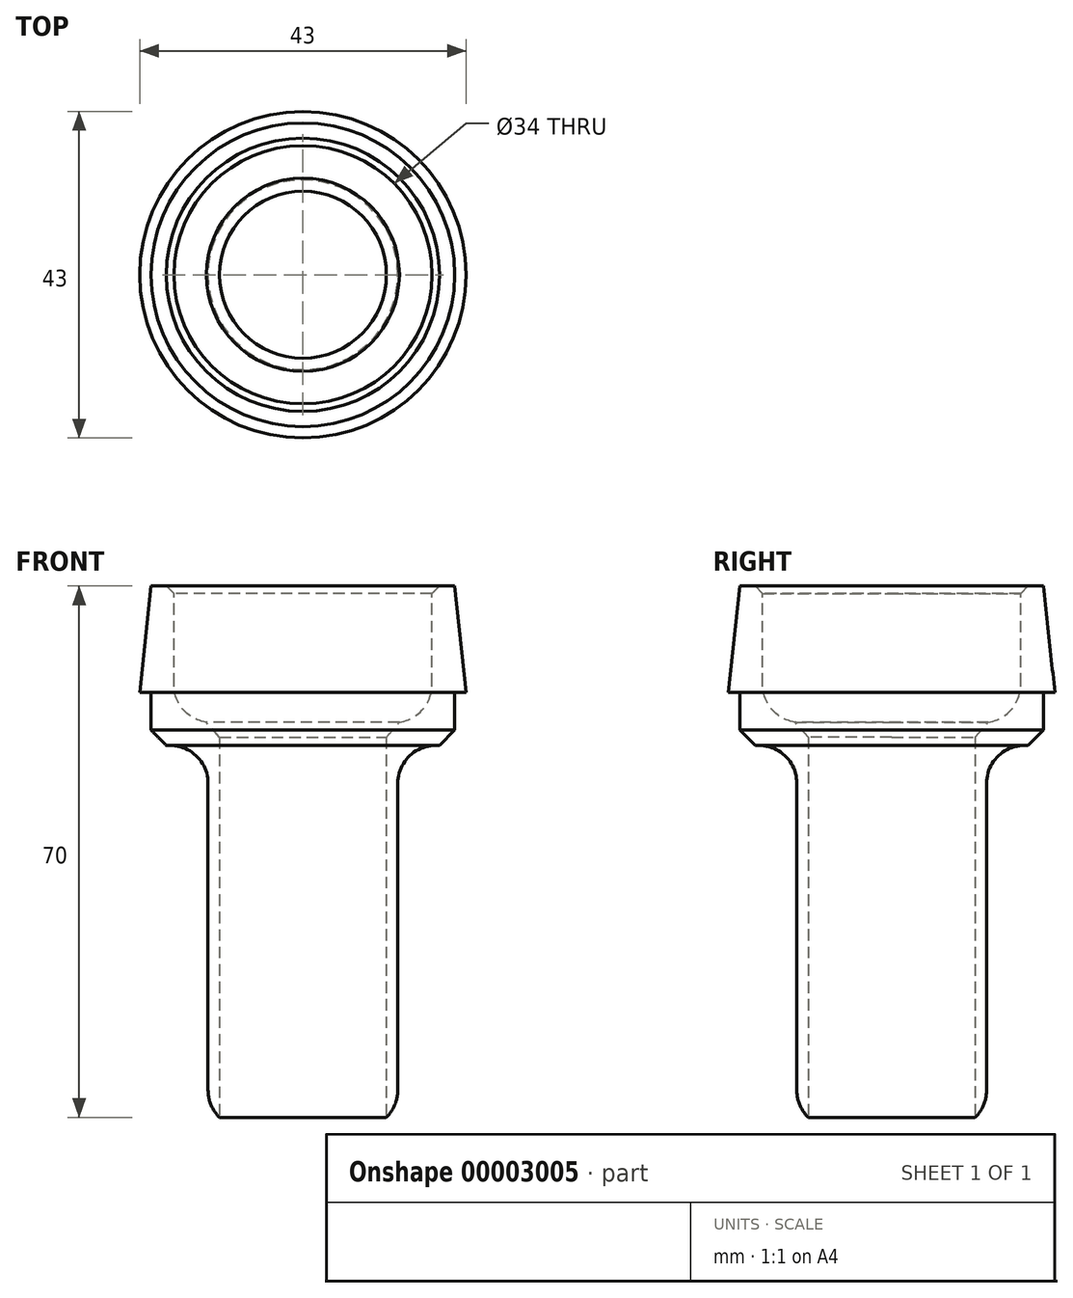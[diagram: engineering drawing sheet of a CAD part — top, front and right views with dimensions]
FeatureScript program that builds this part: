
annotation { "Feature Type Name" : "Feature", "Feature Type Description" : "" }
export const myFeature = defineFeature(function(context is Context, id is Id, definition is map)
    precondition{}
    {
        {
            var Q0;
            Q0=qCreatedBy(makeId("Top.planeOp"),FACE);
            var sketch = newSketch(context, id + "F0", { "sketchPlane" : qUnion([Q0])});
            skCircle(sketch, "E0", {"center": v(0, 0) * mm, "radius": 12.5 * mm});
            skCircle(sketch, "E1", {"center": v(0, 0) * mm, "radius": 11 * mm});
            skSolve(sketch);
        }
        {
            var Q0;
            Q0=makeQuery(id+"F0.imprint","IMPRINT",FACE,{"disambiguationData":[TD([[makeQuery(id+"F0.imprint","IMPRINT",EDGE,{"derivedFrom":sQuery(id+"F0.wireOp",EDGE,"E0")}),1.0]])]});
            extrude(context, id + "F1", {"entities" : qUnion([Q0]), "depth" : 50 * mm});
        }
        {
            var Q0;
            Q0=qCreatedBy(makeId("Right.planeOp"),FACE);
            var sketch = newSketch(context, id + "F2", { "sketchPlane" : qUnion([Q0])});
            skLineSegment(sketch, "E2.0", {"start": v(-12.5, 50) * mm, "end": v(12.5, 50) * mm});
            skLineSegment(sketch, "E3", {"start": v(12.5, 50) * mm, "end": v(0, 50) * mm});
            skLineSegment(sketch, "E4.bottom", {"start": v(0, 50) * mm, "end": v(20, 50) * mm, "construction": true});
            skLineSegment(sketch, "E4.top", {"start": v(0, 56) * mm, "end": v(20, 56) * mm, "construction": true});
            skLineSegment(sketch, "E4.left", {"start": v(0, 50) * mm, "end": v(0, 56) * mm, "construction": true});
            skLineSegment(sketch, "E4.right", {"start": v(20, 50) * mm, "end": v(20, 56) * mm, "construction": true});
            skLineSegment(sketch, "E5.bottom", {"start": v(0, 56) * mm, "end": v(21.5, 56) * mm, "construction": true});
            skLineSegment(sketch, "E5.top", {"start": v(0, 70) * mm, "end": v(21.5, 70) * mm, "construction": true});
            skLineSegment(sketch, "E5.left", {"start": v(0, 56) * mm, "end": v(0, 70) * mm, "construction": true});
            skLineSegment(sketch, "E5.right", {"start": v(21.5, 56) * mm, "end": v(21.5, 70) * mm, "construction": true});
            skLineSegment(sketch, "E6", {"start": v(12.5, 50) * mm, "end": v(20, 50) * mm});
            skLineSegment(sketch, "E7", {"start": v(20, 56) * mm, "end": v(21.5, 56) * mm});
            skLineSegment(sketch, "E8", {"start": v(20, 50) * mm, "end": v(20, 56) * mm});
            skLineSegment(sketch, "E9", {"start": v(21.5, 56) * mm, "end": v(20, 70) * mm});
            skLineSegment(sketch, "E10", {"start": v(20, 70) * mm, "end": v(12.5, 70) * mm});
            skLineSegment(sketch, "E11", {"start": v(12.5, 70) * mm, "end": v(12.5, 50) * mm});
            skLineSegment(sketch, "E12", {"start": v(17, 68.77) * mm, "end": v(17, 71.19) * mm, "construction": true});
            skLineSegment(sketch, "E13", {"start": v(21.07, 52) * mm, "end": v(17.34, 52) * mm, "construction": true});
            skLineSegment(sketch, "E14", {"start": v(17, 70) * mm, "end": v(17, 52) * mm});
            skLineSegment(sketch, "E15", {"start": v(17, 52) * mm, "end": v(12.5, 52) * mm});
            skLineSegment(sketch, "E16", {"start": v(20, 50) * mm, "end": v(20, 49) * mm});
            skLineSegment(sketch, "E17", {"start": v(20, 49) * mm, "end": v(12.5, 49) * mm});
            skLineSegment(sketch, "E18", {"start": v(12.5, 49) * mm, "end": v(12.5, 50) * mm});
            skLineSegment(sketch, "E19", {"start": v(12.5, 52) * mm, "end": v(11, 52) * mm});
            skLineSegment(sketch, "E20", {"start": v(11, 52) * mm, "end": v(11, 50) * mm});
            skLineSegment(sketch, "E21", {"start": v(11, 50) * mm, "end": v(12.5, 50) * mm});
            skSolve(sketch);
        }
        {
            var Q0;
            {var subQ3=sQuery(id+"F2.wireOp",EDGE,"E6");Q0=makeQuery(id+"F2.imprint","IMPRINT",FACE,{"disambiguationData":[TD([[makeQuery(id+"F2.imprint","IMPRINT",EDGE,{"derivedFrom":subQ3}),1.0]])]});}
            var Q1;
            Q1=makeQuery(id+"F2.imprint","IMPRINT",FACE,{"disambiguationData":[TD([[makeQuery(id+"F2.imprint","IMPRINT",EDGE,{"derivedFrom":sQuery(id+"F2.wireOp",EDGE,"E6")}),-1.0]])]});
            var Q2;
            {var subQ1=sQuery(id+"F2.wireOp",EDGE,"E19");Q2=makeQuery(id+"F2.imprint","IMPRINT",FACE,{"disambiguationData":[TD([[makeQuery(id+"F2.imprint","IMPRINT",EDGE,{"derivedFrom":subQ1}),1.0]])]});}
            var Q3;
            Q3=makeQuery(id+"F1.opExtrude","CAP_EDGE",EDGE,{"disambiguationData":[OSD([sQuery(id+"F0.wireOp",EDGE,"E1")])],"isStart":false});
            sweep(context, id + "F3", {"operationType" : NewBodyOperationType.ADD, "profiles" : qUnion([Q0, Q1, Q2]), "path" : qUnion([Q3])});
        }
        {
            var Q0;
            Q0=makeQuery(id+"F1.opExtrude","SWEPT_FACE",FACE,{"disambiguationData":[OSD([sQuery(id+"F0.wireOp",EDGE,"E0")])]});
            var Q1;
            Q1=makeQuery(id+"F3.opSweep","SWEPT_EDGE",EDGE,{"disambiguationData":[OSD([sQuery(id+"F0.wireOp",EDGE,"E1"),sQuery(id+"F2.wireOp",EDGE,"E14"),sQuery(id+"F2.wireOp",EDGE,"E15")])]});
            fillet(context, id + "F4", {"entities" : qUnion([Q0, Q1]), "radius" : 5 * mm, "tangentPropagation" : true, "allowEdgeOverflow" : false});
        }
        {
            var Q0;
            Q0=makeQuery(id+"F3.opSweep","SWEPT_EDGE",EDGE,{"disambiguationData":[OSD([sQuery(id+"F0.wireOp",EDGE,"E1"),sQuery(id+"F2.wireOp",EDGE,"E19"),sQuery(id+"F2.wireOp",EDGE,"E20")])]});
            chamfer(context, id + "F5", {"entities" : qUnion([Q0]), "width" : 2 * mm, "tangentPropagation" : true});
        }
        {
            var Q0;
            Q0=makeQuery(id+"F3.opSweep","SWEPT_EDGE",EDGE,{"disambiguationData":[OSD([sQuery(id+"F0.wireOp",EDGE,"E1"),sQuery(id+"F2.wireOp",EDGE,"E10"),sQuery(id+"F2.wireOp",EDGE,"E14")])]});
            chamfer(context, id + "F6", {"entities" : qUnion([Q0]), "width" : 1 * mm, "tangentPropagation" : true});
        }
        {
            var Q0;
            Q0=makeQuery(id+"F3.opSweep","SWEPT_EDGE",EDGE,{"disambiguationData":[OSD([sQuery(id+"F0.wireOp",EDGE,"E1"),sQuery(id+"F2.wireOp",EDGE,"E16"),sQuery(id+"F2.wireOp",EDGE,"E17")])]});
            chamfer(context, id + "F7", {"entities" : qUnion([Q0]), "width" : 2 * mm, "tangentPropagation" : true});
        }
    });
